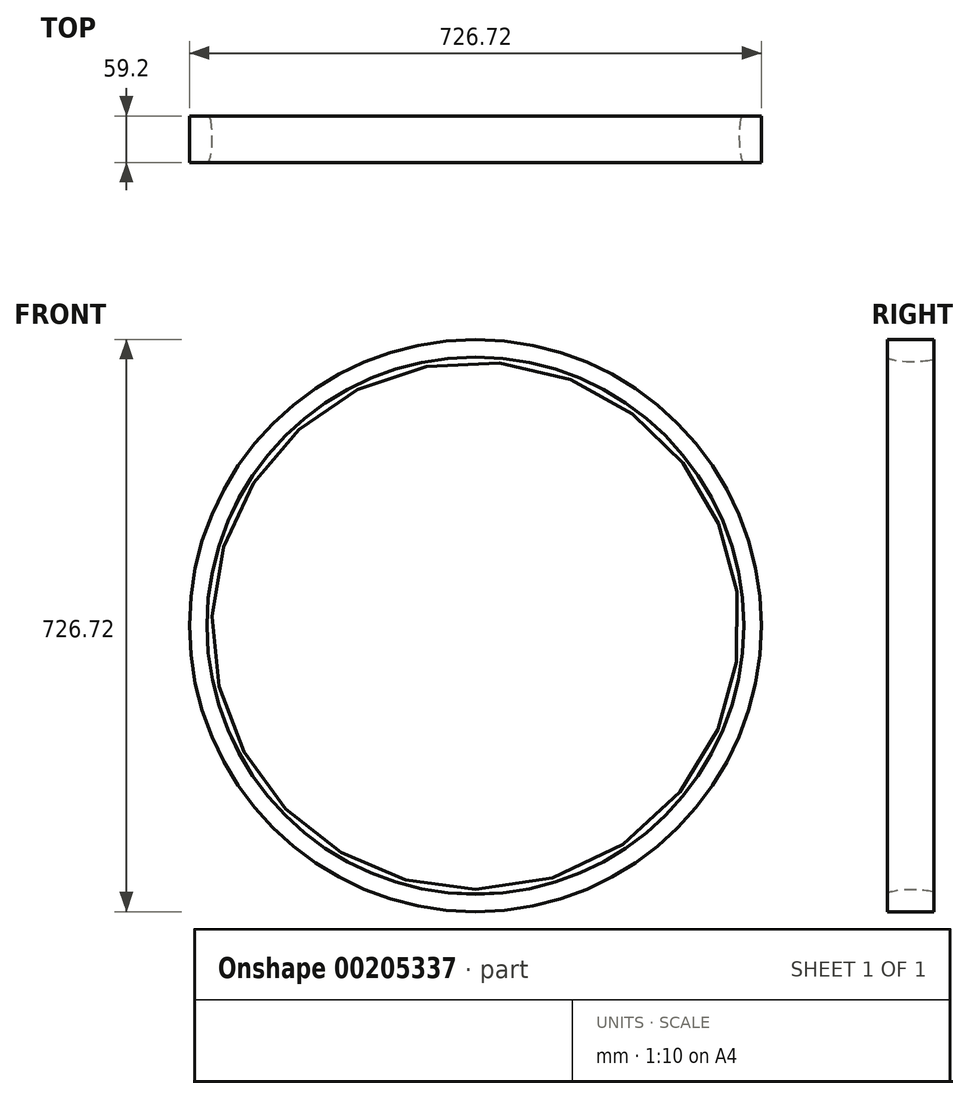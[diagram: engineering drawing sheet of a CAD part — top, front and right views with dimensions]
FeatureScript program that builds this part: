
annotation { "Feature Type Name" : "Feature", "Feature Type Description" : "" }
export const myFeature = defineFeature(function(context is Context, id is Id, definition is map)
    precondition{}
    {
        {
            var Q0;
            Q0=qCreatedBy(makeId("Front.planeOp"),FACE);
            var sketch = newSketch(context, id + "F0", { "sketchPlane" : qUnion([Q0])});
            skCircle(sketch, "E0", {"center": v(0, 0) * mm, "radius": 363.36 * mm});
            skCircle(sketch, "E1", {"center": v(0, 0) * mm, "radius": 334.7 * mm});
            skSolve(sketch);
        }
        {
            var Q0;
            Q0 = qSketchRegion(id + "F0", true);
            extrude(context, id + "F1", {"entities" : qUnion([Q0]), "depth" : 59.2 * mm});
        }
        {
            var Q0;
            Q0=qCreatedBy(makeId("Top.planeOp"),FACE);
            var sketch = newSketch(context, id + "F2", { "sketchPlane" : qUnion([Q0])});
            skPoint(sketch, "E2", {"position": v(-341.1, -27.7) * mm});
            skLineSegment(sketch, "E3", {"start": v(-341.1, -27.7) * mm, "end": v(-341.1, -59.15) * mm});
            skEllipticalArc(sketch, "E4", {});
            skLineSegment(sketch, "E5", {"start": v(-341.1, -59.15) * mm, "end": v(-346.75, -65.43) * mm});
            skLineSegment(sketch, "E6", {"start": v(-346.75, -65.43) * mm, "end": v(-320.8, -65.43) * mm});
            skLineSegment(sketch, "E7", {"start": v(-320.8, -65.43) * mm, "end": v(-323.89, -5.72) * mm});
            skLineSegment(sketch, "E8", {"start": v(334.7, 0) * mm, "end": v(334.7, -59.2) * mm});
            skLineSegment(sketch, "E9", {"start": v(-334.7, -59.2) * mm, "end": v(-334.7, 0) * mm});
            skLineSegment(sketch, "E10", {"start": v(-323.89, -5.72) * mm, "end": v(-336.18, 6.86) * mm});
            skLineSegment(sketch, "E11", {"start": v(-336.18, 6.86) * mm, "end": v(-339.94, 3.19) * mm});
            skPoint(sketch, "E12.end.orphan", {"position": v(-334.93, -27.7) * mm});
            skLineSegment(sketch, "E13", {"start": v(0, 0) * mm, "end": v(0, -121.9) * mm});
            const initialGuessF2  = {"E4": [-0.3411, -0.02770399302244186, 0, -1, 0.03144923970103264, 0.0061659441947937155, 0, 2.952591086134497]};
            skSetInitialGuess(sketch, initialGuessF2);
            skSolve(sketch);
        }
        {
            var Q0;
            Q0=makeQuery(id+"F2.imprint","IMPRINT",FACE,{"disambiguationData":[TD([[makeQuery(id+"F2.imprint","IMPRINT",EDGE,{"derivedFrom":sQuery(id+"F2.wireOp",EDGE,"E4")}),-1.0]])]});
            var Q1;
            Q1=sQuery(id+"F2.wireOp",EDGE,"E13");
            revolve(context, id + "F3", {"operationType" : NewBodyOperationType.REMOVE, "entities" : qUnion([Q0]), "axis" : qUnion([Q1]), "revolveType" : RevolveType.FULL, "oppositeDirection" : true});
        }
        {
            var Q0;
            Q0=makeQuery(id+"F3.boolean.opBoolean","INTERSECT",EDGE,{"derivedFrom":[makeQuery(id+"F1.opExtrude","CAP_FACE",FACE,{"disambiguationData":[OSD([sQuery(id+"F0.wireOp",EDGE,"E0"),sQuery(id+"F0.wireOp",EDGE,"E1")])],"isStart":true}),makeQuery(id+"F3.opRevolve","SWEPT_FACE",FACE,{"disambiguationData":[OSD([sQuery(id+"F2.wireOp",EDGE,"E4")])]})]});
            fillet(context, id + "F4", {"entities" : qUnion([Q0]), "radius" : 3.2 * mm, "tangentPropagation" : true, "allowEdgeOverflow" : false});
        }
    });
